# Revit family: Sanitary_Wash-basins_hansgrohe_60133XXX-CapeTide-Q-Washbasin-600-480-wi__
name_source: partatom
category: Plumbing Fixtures
revit_build: Autodesk Revit 2018 (Build: 20170223_1515(x64)
units: mm (PartAtom-declared; Revit-internal decimal feet)

## family parameters
Always vertical = No
Cut with Voids When Loaded = No
OmniClass Number = 23.31.13.00
OmniClass Title = Sinks
Part Type = Normal
Room Calculation Point = No
Round Connector Dimension = Use Diameter
Shared = No
Work Plane-Based = Yes

## types (1)
- 450 White
    Always visible = Yes
    BIMobject category = Wash basins
    Connector Description = Water Outlet 46 mm
    Default Elevation = 1219.2 mm  [stored 4 ft]
    Description = CapeTide Q Washbasin 600/480 with tap hole and overflow
    Design country = Germany
    Diameter = 46 mm
    EAN code = 4059625478899
    Edition number = 1
    GTIN code = https://4059625478899
    IFC Classification = Sanitary Terminal
    Manufacturer = Hansgrohe
    Manufacturer country = Germany
    Manufacturer name = hansgrohe
    Masterformat 2014 Code = 22 41 16.13
    Masterformat 2014 Description = Residential Lavatories
    Material 1 = Hansgrohe - Ceramic - 450 White
    Model = 60133XXX
    OmniClass Code = 23-31 13 00
    OmniClass Description = Sinks
    Product Guid = 2077f06f-faa5-4f01-8684-41c6b3032291
    Product SKU = 60133XXX
    Product data url = https://bimobject.com
    Product family = CapeTide Q
    Product group = Washbasins
    Product name = 60133XXX CapeTide Q Washbasin 600/480 with tap hole and overflow
    Product url = https://pro.hansgrohe.com
    QR code = https://bimobject.com
    UNSPSC Code = 301815
    URL = https://www.hansgrohe.com
    Uniclass 2015 Code = Pr_40_20_96
    Uniclass 2015 Name = Wash basins, sinks and troughs
    Uniformat II Code = D2010
    Uniformat II Description = Plumbing Fixtures
    Weight Net (Kg) = 17,7

note: [stored X ft] marks values corroborated as IEEE doubles in the binary element streams (Revit-internal decimal feet)

## geometry (parser evidence)
native form markers: Sweep x2
no freeform markers — native parametric forms only
